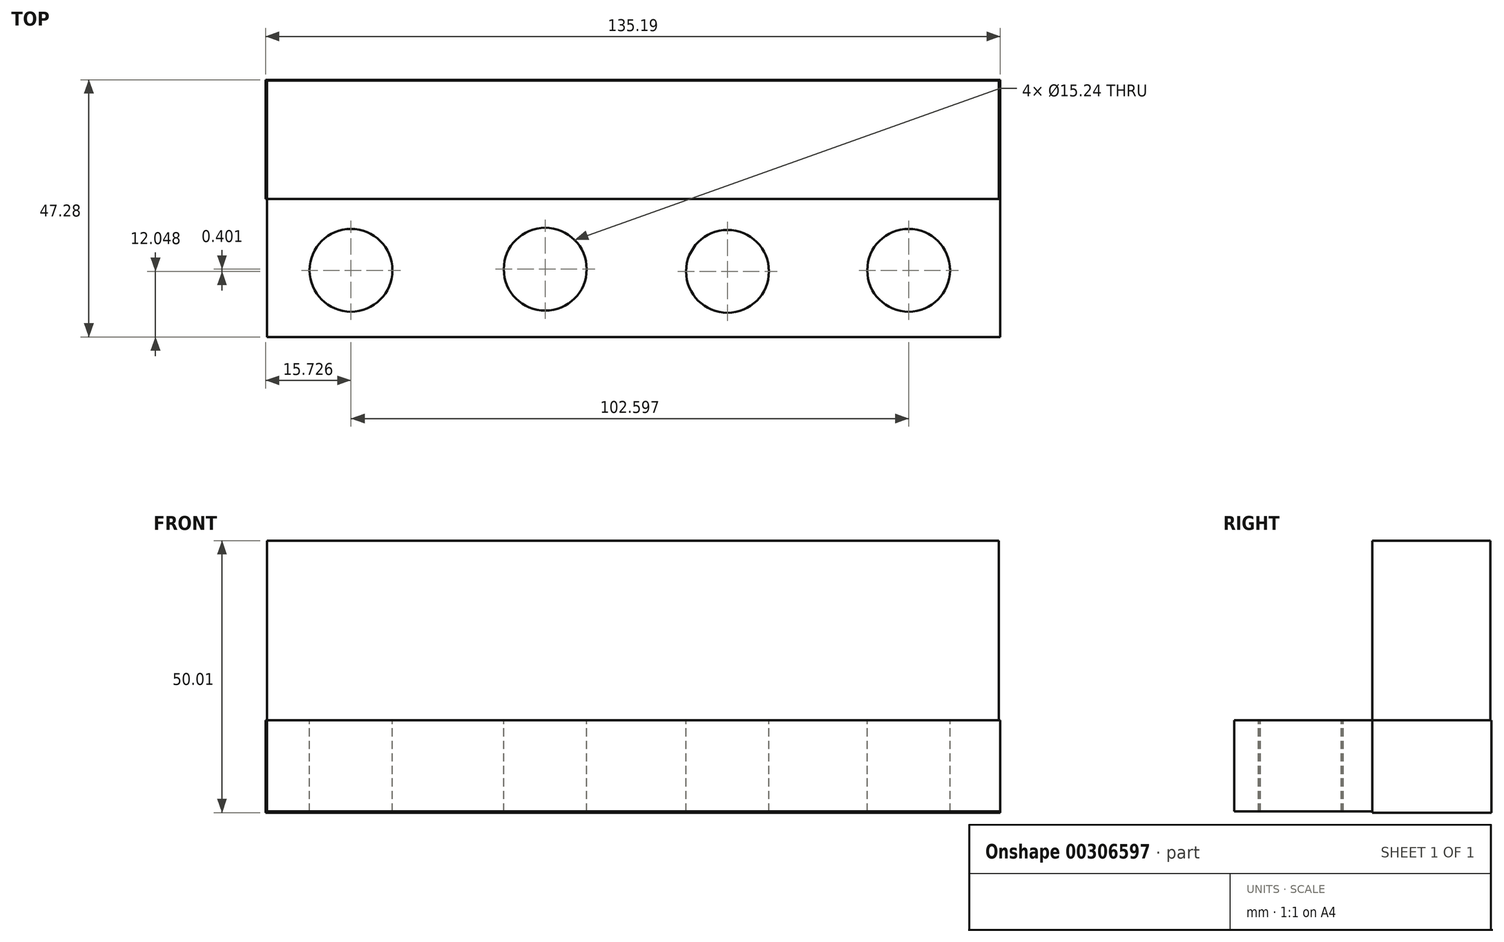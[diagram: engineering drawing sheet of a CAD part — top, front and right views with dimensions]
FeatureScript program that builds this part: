
annotation { "Feature Type Name" : "Feature", "Feature Type Description" : "" }
export const myFeature = defineFeature(function(context is Context, id is Id, definition is map)
    precondition{}
    {
        {
            var Q0;
            Q0=qCreatedBy(makeId("Front.planeOp"),FACE);
            var sketch = newSketch(context, id + "F0", { "sketchPlane" : qUnion([Q0])});
            skLineSegment(sketch, "E0.bottom", {"start": v(-68.06, 0) * mm, "end": v(66.86, 0) * mm});
            skLineSegment(sketch, "E0.top", {"start": v(-68.06, -16.76) * mm, "end": v(66.86, -16.76) * mm});
            skLineSegment(sketch, "E0.left", {"start": v(-68.06, 0) * mm, "end": v(-68.06, -16.76) * mm});
            skLineSegment(sketch, "E0.right", {"start": v(66.86, 0) * mm, "end": v(66.86, -16.76) * mm});
            skLineSegment(sketch, "E1.top", {"start": v(-68.06, 35.84) * mm, "end": v(66.86, 35.84) * mm});
            skLineSegment(sketch, "E1.left", {"start": v(-68.06, 0) * mm, "end": v(-68.06, 35.84) * mm});
            skLineSegment(sketch, "E1.right", {"start": v(66.86, 0) * mm, "end": v(66.86, 35.84) * mm});
            skSolve(sketch);
        }
        {
            var Q0;
            Q0=makeQuery(id+"F0.imprint","IMPRINT",FACE,{"disambiguationData":[TD([[makeQuery(id+"F0.imprint","IMPRINT",EDGE,{"derivedFrom":sQuery(id+"F0.wireOp",EDGE,"E0.top")}),1.0]])]});
            extrude(context, id + "F1", {"entities" : qUnion([Q0]), "depth" : 25.4 * mm});
        }
        {
            var Q0;
            Q0=qCreatedBy(makeId("Right.planeOp"),FACE);
            var sketch = newSketch(context, id + "F2", { "sketchPlane" : qUnion([Q0])});
            skLineSegment(sketch, "E2.bottom", {"start": v(0, 0) * mm, "end": v(21.88, 0) * mm});
            skLineSegment(sketch, "E2.top", {"start": v(0, -16.97) * mm, "end": v(21.88, -16.97) * mm});
            skLineSegment(sketch, "E2.left", {"start": v(0, 0) * mm, "end": v(0, -16.97) * mm});
            skLineSegment(sketch, "E2.right", {"start": v(21.88, 0) * mm, "end": v(21.88, -16.97) * mm});
            skSolve(sketch);
        }
        {
            var Q0;
            Q0=makeQuery(id+"F2.imprint","IMPRINT",FACE,{"disambiguationData":[TD([[makeQuery(id+"F2.imprint","IMPRINT",EDGE,{"derivedFrom":sQuery(id+"F2.wireOp",EDGE,"E2.bottom")}),-1.0]])]});
            extrude(context, id + "F3", {"entities" : qUnion([Q0]), "operationType" : NewBodyOperationType.ADD, "depth" : 25.4 * mm});
        }
        {
            var Q0;
            Q0=makeQuery(id+"F3.opExtrude","CAP_FACE",FACE,{"disambiguationData":[OSD([sQuery(id+"F2.wireOp",EDGE,"E2.bottom"),sQuery(id+"F2.wireOp",EDGE,"E2.top"),sQuery(id+"F2.wireOp",EDGE,"E2.left"),sQuery(id+"F2.wireOp",EDGE,"E2.right")])],"isStart":false});
            extrude(context, id + "F4", {"entities" : qUnion([Q0]), "operationType" : NewBodyOperationType.ADD, "depth" : 25.4 * mm});
        }
        {
            var Q0;
            Q0=makeQuery(id+"F4.opExtrude","CAP_FACE",FACE,{"disambiguationData":[OSD([sQuery(id+"F2.wireOp",EDGE,"E2.bottom"),sQuery(id+"F2.wireOp",EDGE,"E2.top"),sQuery(id+"F2.wireOp",EDGE,"E2.left"),sQuery(id+"F2.wireOp",EDGE,"E2.right")])],"isStart":false});
            extrude(context, id + "F5", {"entities" : qUnion([Q0]), "operationType" : NewBodyOperationType.ADD, "depth" : 16 * mm});
        }
        {
            var Q0;
            Q0=makeQuery(id+"F3.opExtrude","CAP_FACE",FACE,{"disambiguationData":[OSD([sQuery(id+"F2.wireOp",EDGE,"E2.bottom"),sQuery(id+"F2.wireOp",EDGE,"E2.top"),sQuery(id+"F2.wireOp",EDGE,"E2.left"),sQuery(id+"F2.wireOp",EDGE,"E2.right")])],"isStart":true});
            extrude(context, id + "F6", {"entities" : qUnion([Q0]), "operationType" : NewBodyOperationType.ADD, "depth" : 68.33 * mm});
        }
        {
            var Q0;
            Q0=qCreatedBy(makeId("Right.planeOp"),FACE);
            var sketch = newSketch(context, id + "F7", { "sketchPlane" : qUnion([Q0])});
            skLineSegment(sketch, "E3.bottom", {"start": v(21.72, 0) * mm, "end": v(0, 0) * mm});
            skLineSegment(sketch, "E3.top", {"start": v(21.72, 33.04) * mm, "end": v(0, 33.04) * mm});
            skLineSegment(sketch, "E3.left", {"start": v(21.72, 0) * mm, "end": v(21.72, 33.04) * mm});
            skLineSegment(sketch, "E3.right", {"start": v(0, 0) * mm, "end": v(0, 33.04) * mm});
            skSolve(sketch);
        }
        {
            var Q0;
            Q0=makeQuery(id+"F7.imprint","IMPRINT",FACE,{"disambiguationData":[TD([[makeQuery(id+"F7.imprint","IMPRINT",EDGE,{"derivedFrom":sQuery(id+"F7.wireOp",EDGE,"E3.bottom")}),-1.0]])]});
            extrude(context, id + "F8", {"entities" : qUnion([Q0]), "operationType" : NewBodyOperationType.ADD, "depth" : 66.55 * mm});
        }
        {
            var Q0;
            Q0=makeQuery(id+"F8.opExtrude","CAP_FACE",FACE,{"disambiguationData":[OSD([sQuery(id+"F7.wireOp",EDGE,"E3.bottom"),sQuery(id+"F7.wireOp",EDGE,"E3.top"),sQuery(id+"F7.wireOp",EDGE,"E3.left"),sQuery(id+"F7.wireOp",EDGE,"E3.right")])],"isStart":true});
            extrude(context, id + "F9", {"entities" : qUnion([Q0]), "operationType" : NewBodyOperationType.ADD, "depth" : 68.07 * mm});
        }
        {
            var Q0;
            {var subQ0=sQuery(id+"F2.wireOp",EDGE,"E2.bottom");Q0=makeQuery(id+"F6.boolean.opBoolean","MERGE",FACE,{"derivedFrom":[makeQuery(id+"F5.boolean.opBoolean","MERGE",FACE,{"derivedFrom":[makeQuery(id+"F4.boolean.opBoolean","MERGE",FACE,{"derivedFrom":[makeQuery(id+"F3.boolean.opBoolean","MERGE",FACE,{"derivedFrom":[makeQuery(id+"F1.opExtrude","SWEPT_FACE",FACE,{"disambiguationData":[OSD([sQuery(id+"F0.wireOp",EDGE,"E0.bottom")])]}),makeQuery(id+"F3.opExtrude","SWEPT_FACE",FACE,{"disambiguationData":[OSD([subQ0])]})]}),makeQuery(id+"F4.opExtrude","SWEPT_FACE",FACE,{"disambiguationData":[OSD([subQ0])]})]}),makeQuery(id+"F5.opExtrude","SWEPT_FACE",FACE,{"disambiguationData":[OSD([subQ0])]})]}),makeQuery(id+"F6.opExtrude","SWEPT_FACE",FACE,{"disambiguationData":[OSD([subQ0])]})]});}
            var sketch = newSketch(context, id + "F10", { "sketchPlane" : qUnion([Q0])});
            skCircle(sketch, "E4", {"center": v(-52.6, -13.15) * mm, "radius": 7.75 * mm});
            skCircle(sketch, "E5", {"center": v(-16.87, -12.95) * mm, "radius": 7.75 * mm});
            skCircle(sketch, "E6", {"center": v(16.66, -13.35) * mm, "radius": 7.75 * mm});
            skCircle(sketch, "E7", {"center": v(50, -13.15) * mm, "radius": 7.75 * mm});
            skSolve(sketch);
        }
        {
            var Q0;
            Q0=sQuery(id+"F10.wireOp",VERTEX,"E4.center");
            var Q1;
            Q1=makeQuery(id+"F1.opExtrude","SWEPT_BODY",BODY,{"disambiguationData":[OSD([sQuery(id+"F0.wireOp",EDGE,"E0.top"),sQuery(id+"F0.wireOp",EDGE,"E0.left"),sQuery(id+"F0.wireOp",EDGE,"E0.right"),sQuery(id+"F0.wireOp",EDGE,"E0.bottom")])]});
            hole(context, id + "F11", {"style" : HoleStyle.SIMPLE, "endStyle" : HoleEndStyle.THROUGH, "holeDiameter" : 15.24 * mm, "tappedDepth" : 12.7 * mm, "tapClearance" : 3, "startFromSketch" : true, "locations" : qUnion([Q0]), "scope" : qUnion([Q1])});
        }
        {
            var Q0;
            Q0=sQuery(id+"F10.wireOp",VERTEX,"E5.center");
            var Q1;
            Q1=makeQuery(id+"F1.opExtrude","SWEPT_BODY",BODY,{"disambiguationData":[OSD([sQuery(id+"F0.wireOp",EDGE,"E0.top"),sQuery(id+"F0.wireOp",EDGE,"E0.left"),sQuery(id+"F0.wireOp",EDGE,"E0.right"),sQuery(id+"F0.wireOp",EDGE,"E0.bottom")])]});
            hole(context, id + "F12", {"style" : HoleStyle.SIMPLE, "endStyle" : HoleEndStyle.THROUGH, "holeDiameter" : 15.24 * mm, "tappedDepth" : 12.7 * mm, "tapClearance" : 3, "startFromSketch" : true, "locations" : qUnion([Q0]), "scope" : qUnion([Q1])});
        }
        {
            var Q0;
            Q0=sQuery(id+"F10.wireOp",VERTEX,"E6.center");
            var Q1;
            Q1=sQuery(id+"F10.wireOp",VERTEX,"E7.center");
            var Q2;
            Q2=makeQuery(id+"F1.opExtrude","SWEPT_BODY",BODY,{"disambiguationData":[OSD([sQuery(id+"F0.wireOp",EDGE,"E0.top"),sQuery(id+"F0.wireOp",EDGE,"E0.left"),sQuery(id+"F0.wireOp",EDGE,"E0.right"),sQuery(id+"F0.wireOp",EDGE,"E0.bottom")])]});
            hole(context, id + "F13", {"style" : HoleStyle.SIMPLE, "endStyle" : HoleEndStyle.THROUGH, "holeDiameter" : 15.24 * mm, "tappedDepth" : 12.7 * mm, "tapClearance" : 3, "startFromSketch" : true, "locations" : qUnion([Q0, Q1]), "scope" : qUnion([Q2])});
        }
    });
